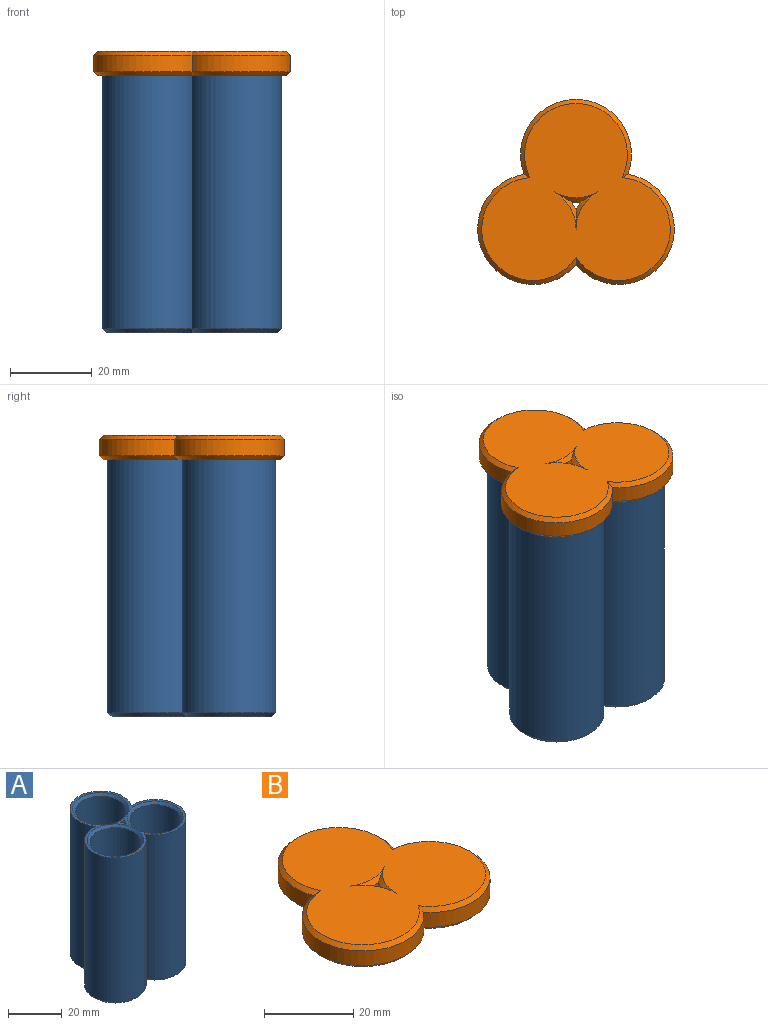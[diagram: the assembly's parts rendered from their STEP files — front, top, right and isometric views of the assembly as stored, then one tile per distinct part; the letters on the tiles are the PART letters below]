
ASSEMBLY  parts=2 mates=1
PART A: 26 faces, bbox 44x41.2x67 mm
  f0: plane 21x21mm, normal (0,0,-1), area 346.4mm2, adj f22,f23
  f1: plane 21x21mm, normal (0,0,-1), area 346.4mm2, adj f21,f24
  f2: plane 44x41.19mm, normal (0,0,1), area 153.9mm2, adj f6,f7,f10,f17,f18,f19
  f3: plane 21x21mm, normal (0,0,-1), area 346.4mm2, adj f20,f25
  f4: cylinder r=11.5mm len=66mm, axis (0,0,1), area 157.1mm2, adj f5,f12,f13,f22
  f5: cylinder r=11.5mm len=66mm, axis (0,0,1), area 157.1mm2, adj f4,f12,f13,f20
  f6: cylinder r=11.5mm len=66mm, axis (0,0,1), area 3336.4mm2, adj f2,f7,f10,f25
  f7: cylinder r=11.5mm len=66mm, axis (0,0,1), area 3336.4mm2, adj f2,f6,f10,f23
  f8: cylinder r=9.5mm len=64mm, axis (0,0,1), area 3820.2mm2, adj f15,f18
  f9: cylinder r=9.5mm len=64mm, axis (0,0,1), area 3820.2mm2, adj f14,f19
  f10: cylinder r=11.5mm len=66mm, axis (0,0,1), area 3336.4mm2, adj f2,f6,f7,f24
  f11: cylinder r=9.5mm len=64mm, axis (0,0,1), area 3820.2mm2, adj f16,f17
  f12: cylinder r=11.5mm len=66mm, axis (0,0,1), area 157.1mm2, adj f4,f5,f13,f21
  f13: plane 10.5x9.09mm, normal (0,0,1), area 15.6mm2, adj f4,f5,f12,f17,f18,f19
  f14: plane 19x19mm, normal (0,0,1), area 283.5mm2, adj f9
  f15: plane 19x19mm, normal (0,0,1), area 283.5mm2, adj f8
  f16: plane 19x19mm, normal (0,0,1), area 283.5mm2, adj f11
  f17: cone r=9.5mm half-angle=45deg, axis (0,0,1), area 88.9mm2, adj f2,f11,f13
  f18: cone r=9.5mm half-angle=45deg, axis (0,0,1), area 88.9mm2, adj f2,f8,f13
  f19: cone r=9.5mm half-angle=45deg, axis (0,0,1), area 88.9mm2, adj f2,f9,f13
  f20: cone r=10.5mm half-angle=45deg, axis (0,0,1), area 7.4mm2, adj f3,f5,f21,f22
  f21: cone r=10.5mm half-angle=45deg, axis (0,0,1), area 7.4mm2, adj f1,f12,f20,f22
  f22: cone r=10.5mm half-angle=45deg, axis (0,0,1), area 7.4mm2, adj f0,f4,f20,f21
  f23: cone r=10.5mm half-angle=45deg, axis (0,0,1), area 72.5mm2, adj f0,f7,f24,f25
  f24: cone r=10.5mm half-angle=45deg, axis (0,0,1), area 72.5mm2, adj f1,f10,f23,f25
  f25: cone r=10.5mm half-angle=45deg, axis (0,0,1), area 72.5mm2, adj f3,f6,f23,f24
PART B: 24 faces, bbox 48.2x45.4x6 mm
  f0: cylinder r=13.6mm len=27.02mm, axis (0,0,-1), area 209.9mm2, adj f1,f5,f12,f15
  f1: cylinder r=13.6mm len=27.2mm, axis (0,0,-1), area 209.9mm2, adj f0,f5,f14,f17
  f2: cylinder r=11.6mm len=23.2mm, axis (0,0,-1), area 176.9mm2, adj f3,f4,f7,f22
  f3: cylinder r=11.6mm len=23.2mm, axis (0,0,-1), area 176.9mm2, adj f2,f4,f7,f23
  f4: cylinder r=11.6mm len=23.2mm, axis (0,0,-1), area 176.9mm2, adj f2,f3,f7,f21
  f5: cylinder r=13.6mm len=27.02mm, axis (0,0,-1), area 209.9mm2, adj f0,f1,f13,f16
  f6: plane 46.2x43.39mm, normal (0,0,-1), area 76.5mm2, adj f12,f13,f14,f21,f22,f23
  f7: plane 44.2x41.39mm, normal (0,0,-1), area 1223.7mm2, adj f2,f3,f4,f8,f9,f10
  f8: cylinder r=11.5mm len=2.38mm, axis (0,0,-1), area 2.4mm2, adj f7,f9,f10,f19
  f9: cylinder r=11.5mm len=2.06mm, axis (0,0,-1), area 2.4mm2, adj f7,f8,f10,f18
  f10: cylinder r=11.5mm len=2.06mm, axis (0,0,-1), area 2.4mm2, adj f7,f8,f9,f20
  f11: plane 46.2x43.39mm, normal (0,0,1), area 1360.5mm2, adj f15,f16,f17,f18,f19,f20
  f12: cone r=13.6mm half-angle=45deg, axis (0,0,1), area 73.4mm2, adj f0,f6,f13,f14
  f13: cone r=13.6mm half-angle=45deg, axis (0,0,1), area 73.4mm2, adj f5,f6,f12,f14
  f14: cone r=13.6mm half-angle=45deg, axis (0,0,1), area 73.4mm2, adj f1,f6,f12,f13
  f15: cone r=12.6mm half-angle=45deg, axis (0,0,-1), area 73.4mm2, adj f0,f11,f16,f17
  f16: cone r=12.6mm half-angle=45deg, axis (0,0,-1), area 73.4mm2, adj f5,f11,f15,f17
  f17: cone r=12.6mm half-angle=45deg, axis (0,0,-1), area 73.4mm2, adj f1,f11,f15,f16
  f18: cone r=10.5mm half-angle=45deg, axis (0,0,-1), area 7.4mm2, adj f9,f11,f19,f20
  f19: cone r=10.5mm half-angle=45deg, axis (0,0,-1), area 7.4mm2, adj f8,f11,f18,f20
  f20: cone r=10.5mm half-angle=45deg, axis (0,0,-1), area 7.4mm2, adj f10,f11,f18,f19
  f21: cone r=12.1mm half-angle=45deg, axis (0,0,-1), area 35.8mm2, adj f4,f6,f22,f23
  f22: cone r=12.1mm half-angle=45deg, axis (0,0,-1), area 35.8mm2, adj f2,f6,f21,f23
  f23: cone r=12.1mm half-angle=45deg, axis (0,0,-1), area 35.8mm2, adj f3,f6,f21,f22
PLACE A t=(0,-12.12,2)mm
PLACE B t=(0,-12.12,-2)mm
MATE slider B.f7 <-> A.f13  axis (0,0,-1) through (0,-12.12,67)mm
